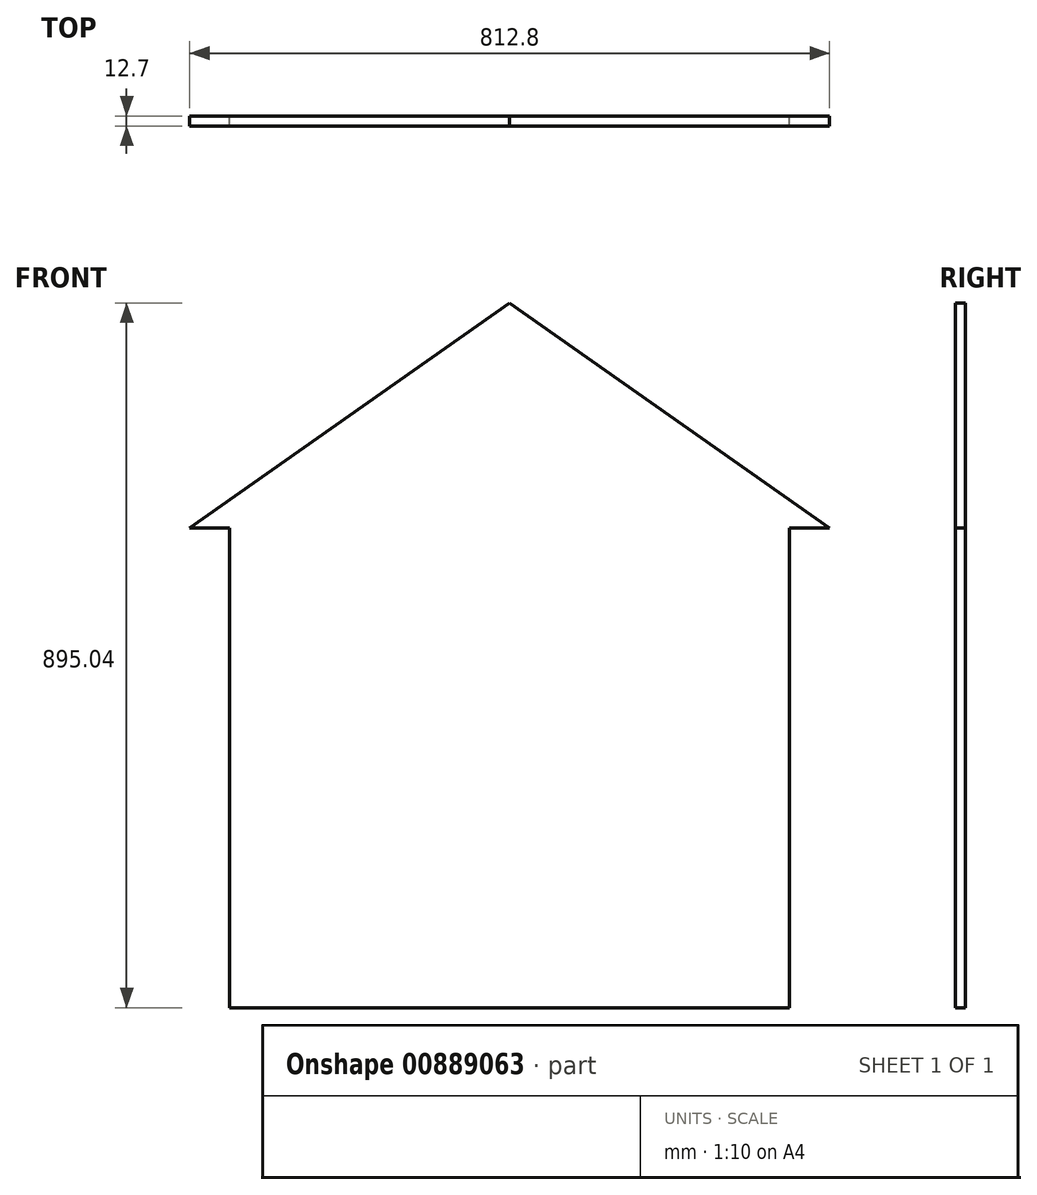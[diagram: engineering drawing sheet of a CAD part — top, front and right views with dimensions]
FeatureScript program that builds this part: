
annotation { "Feature Type Name" : "Feature", "Feature Type Description" : "" }
export const myFeature = defineFeature(function(context is Context, id is Id, definition is map)
    precondition{}
    {
        {
            var Q0;
            Q0=qCreatedBy(makeId("Front.planeOp"),FACE);
            var sketch = newSketch(context, id + "F0", { "sketchPlane" : qUnion([Q0])});
            skLineSegment(sketch, "E0.top", {"start": v(-355.6, -304.8) * mm, "end": v(355.6, -304.8) * mm});
            skLineSegment(sketch, "E0.left", {"start": v(-355.6, 304.8) * mm, "end": v(-355.6, -304.8) * mm});
            skLineSegment(sketch, "E0.right", {"start": v(355.6, 304.8) * mm, "end": v(355.6, -304.8) * mm});
            skPoint(sketch, "E0.middle", {"position": v(0, 0) * mm});
            skLineSegment(sketch, "E1", {"start": v(-406.4, 304.8) * mm, "end": v(-355.6, 304.8) * mm});
            skLineSegment(sketch, "E2", {"start": v(355.6, 304.8) * mm, "end": v(406.4, 304.8) * mm});
            skLineSegment(sketch, "E3", {"start": v(-406.4, 304.8) * mm, "end": v(0, 590.24) * mm});
            skLineSegment(sketch, "E4", {"start": v(0, 590.24) * mm, "end": v(406.4, 304.8) * mm});
            skPoint(sketch, "E5", {"position": v(0, 304.8) * mm});
            skSolve(sketch);
        }
        {
            var Q0;
            Q0 = qSketchRegion(id + "F0", true);
            extrude(context, id + "F1", {"entities" : qUnion([Q0]), "depth" : 12.7 * mm, "offsetDistance" : 25.4 * mm});
        }
    });
